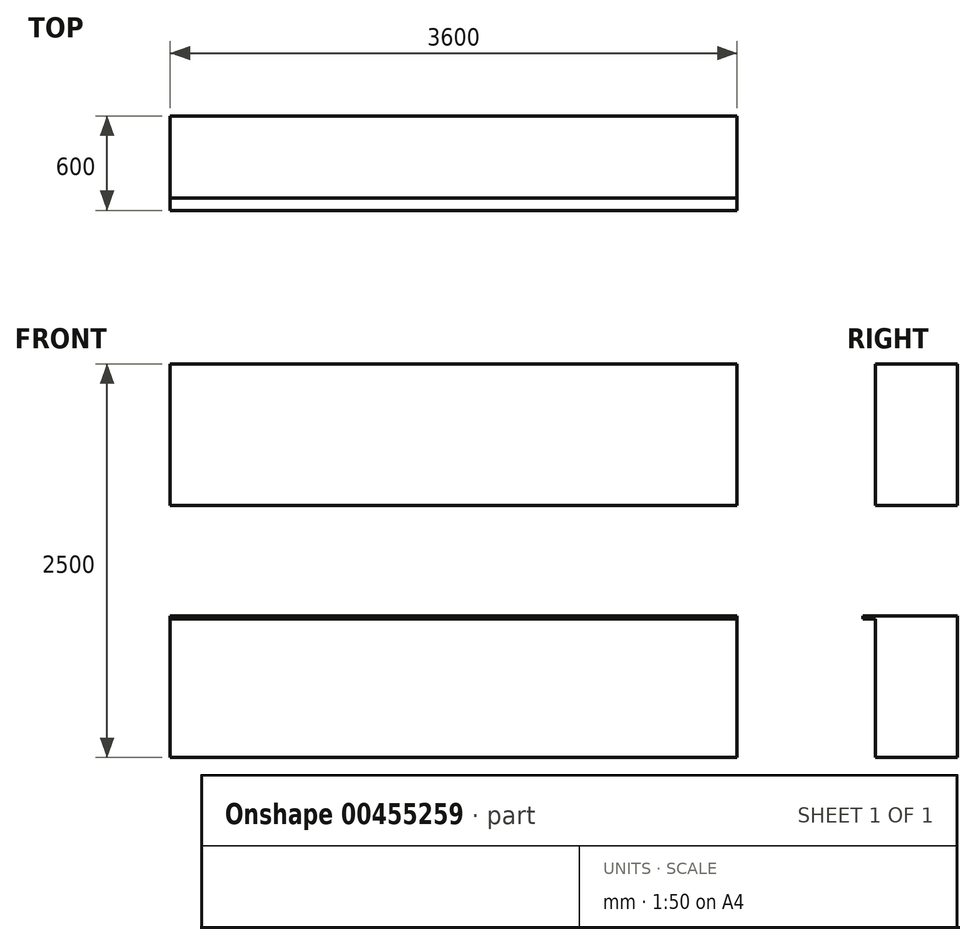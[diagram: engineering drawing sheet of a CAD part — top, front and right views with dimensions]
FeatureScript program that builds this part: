
annotation { "Feature Type Name" : "Feature", "Feature Type Description" : "" }
export const myFeature = defineFeature(function(context is Context, id is Id, definition is map)
    precondition{}
    {
        {
            var Q0;
            Q0=qCreatedBy(makeId("Top.planeOp"),FACE);
            var sketch = newSketch(context, id + "F0", { "sketchPlane" : qUnion([Q0])});
            skLineSegment(sketch, "E0.bottom", {"start": v(-1797.87, 208.45) * mm, "end": v(1802.13, 208.45) * mm});
            skLineSegment(sketch, "E0.top", {"start": v(-1797.87, -391.55) * mm, "end": v(1802.13, -391.55) * mm});
            skLineSegment(sketch, "E0.left", {"start": v(-1797.87, 208.45) * mm, "end": v(-1797.87, -391.55) * mm});
            skLineSegment(sketch, "E0.right", {"start": v(1802.13, 208.45) * mm, "end": v(1802.13, -391.55) * mm});
            skLineSegment(sketch, "E1", {"start": v(-1797.87, -311.55) * mm, "end": v(1802.13, -311.55) * mm});
            skSolve(sketch);
        }
        {
            var Q0;
            {var subQ0=sQuery(id+"F0.wireOp",EDGE,"E0.bottom");Q0=makeQuery(id+"F0.imprint","IMPRINT",FACE,{"disambiguationData":[TD([[makeQuery(id+"F0.imprint","IMPRINT",EDGE,{"derivedFrom":subQ0}),-1.0]])]});}
            extrude(context, id + "F1", {"entities" : qUnion([Q0]), "depth" : 880 * mm, "offsetDistance" : 25 * mm});
        }
        {
            var Q0;
            {var subQ0=sQuery(id+"F0.wireOp",EDGE,"E0.bottom");Q0=makeQuery(id+"F0.imprint","IMPRINT",FACE,{"disambiguationData":[TD([[makeQuery(id+"F0.imprint","IMPRINT",EDGE,{"derivedFrom":subQ0}),-1.0]])]});}
            var Q1;
            {var subQ0=sQuery(id+"F0.wireOp",EDGE,"E0.top");Q1=makeQuery(id+"F0.imprint","IMPRINT",FACE,{"disambiguationData":[TD([[makeQuery(id+"F0.imprint","IMPRINT",EDGE,{"derivedFrom":subQ0}),1.0]])]});}
            extrude(context, id + "F2", {"entities" : qUnion([Q0, Q1]), "operationType" : NewBodyOperationType.ADD, "depth" : 900 * mm, "offsetDistance" : 25 * mm, "hasSecondDirection" : true, "secondDirectionOppositeDirection" : false, "secondDirectionDepth" : 880 * mm});
        }
        {
            var Q0;
            {var subQ0=sQuery(id+"F0.wireOp",EDGE,"E0.bottom");Q0=makeQuery(id+"F0.imprint","IMPRINT",FACE,{"disambiguationData":[TD([[makeQuery(id+"F0.imprint","IMPRINT",EDGE,{"derivedFrom":subQ0}),-1.0]])]});}
            extrude(context, id + "F3", {"entities" : qUnion([Q0]), "depth" : 2500 * mm, "offsetDistance" : 25 * mm, "hasSecondDirection" : true, "secondDirectionOppositeDirection" : false, "secondDirectionDepth" : 1600 * mm});
        }
    });
